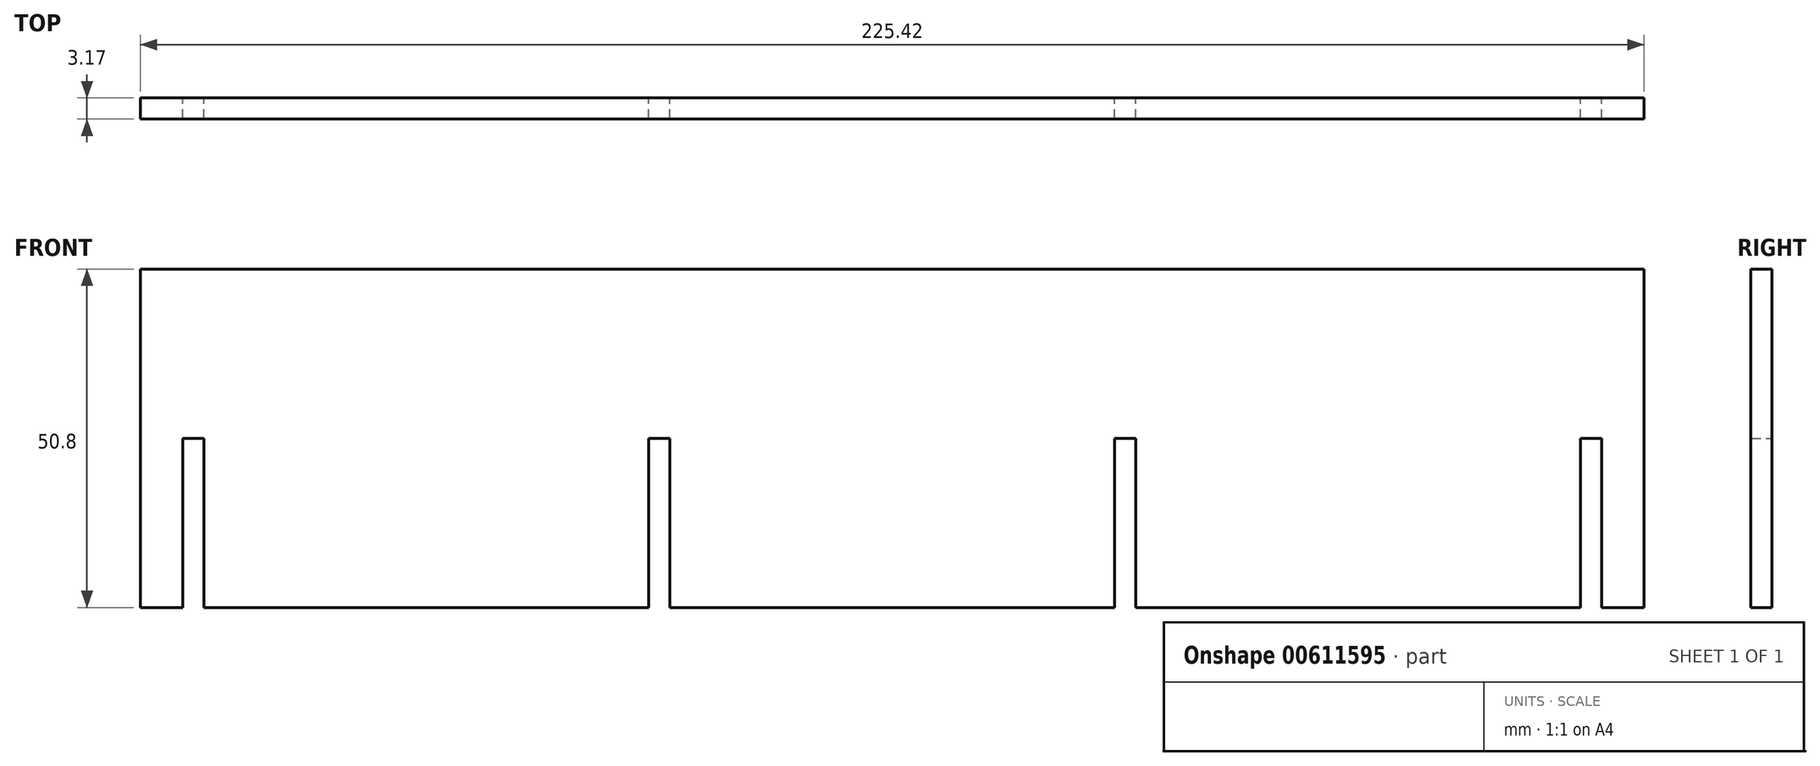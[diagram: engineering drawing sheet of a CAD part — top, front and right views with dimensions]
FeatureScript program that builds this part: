
annotation { "Feature Type Name" : "Feature", "Feature Type Description" : "" }
export const myFeature = defineFeature(function(context is Context, id is Id, definition is map)
    precondition{}
    {
        {
            var Q0;
            Q0=qCreatedBy(makeId("Front.planeOp"),FACE);
            var sketch = newSketch(context, id + "F0", { "sketchPlane" : qUnion([Q0])});
            skLineSegment(sketch, "E0.bottom", {"start": v(-112.71, 25.4) * mm, "end": v(112.71, 25.4) * mm});
            skLineSegment(sketch, "E0.top", {"start": v(-112.71, -25.4) * mm, "end": v(112.71, -25.4) * mm});
            skLineSegment(sketch, "E0.left", {"start": v(-112.71, 25.4) * mm, "end": v(-112.71, -25.4) * mm});
            skLineSegment(sketch, "E0.right", {"start": v(112.71, 25.4) * mm, "end": v(112.71, -25.4) * mm});
            skPoint(sketch, "E0.middle", {"position": v(0, 0) * mm});
            skLineSegment(sketch, "E1", {"start": v(-106.36, -25.4) * mm, "end": v(-106.36, 0) * mm});
            skLineSegment(sketch, "E2", {"start": v(-106.36, 0) * mm, "end": v(-103.19, 0) * mm});
            skLineSegment(sketch, "E3", {"start": v(-103.19, 0) * mm, "end": v(-103.19, -25.4) * mm});
            skLineSegment(sketch, "E4", {"start": v(-36.51, -25.4) * mm, "end": v(-36.51, 0) * mm});
            skLineSegment(sketch, "E5", {"start": v(-36.51, 0) * mm, "end": v(-33.34, 0) * mm});
            skLineSegment(sketch, "E6", {"start": v(-33.34, 0) * mm, "end": v(-33.34, -25.4) * mm});
            skLineSegment(sketch, "E7", {"start": v(33.34, -25.4) * mm, "end": v(33.34, 0) * mm});
            skLineSegment(sketch, "E8", {"start": v(33.34, 0) * mm, "end": v(36.51, 0) * mm});
            skLineSegment(sketch, "E9", {"start": v(36.51, 0) * mm, "end": v(36.51, -25.4) * mm});
            skLineSegment(sketch, "E10", {"start": v(103.19, -25.4) * mm, "end": v(103.19, 0) * mm});
            skLineSegment(sketch, "E11", {"start": v(103.19, 0) * mm, "end": v(106.36, 0) * mm});
            skLineSegment(sketch, "E12", {"start": v(106.36, 0) * mm, "end": v(106.36, -25.4) * mm});
            skSolve(sketch);
        }
        {
            var Q0;
            Q0=makeQuery(id+"F0.imprint","IMPRINT",FACE,{"disambiguationData":[TD([[makeQuery(id+"F0.imprint","IMPRINT",EDGE,{"derivedFrom":sQuery(id+"F0.wireOp",EDGE,"E0.bottom")}),-1.0]])]});
            extrude(context, id + "F1", {"entities" : qUnion([Q0]), "depth" : 3.17 * mm, "offsetDistance" : 25.4 * mm});
        }
    });
